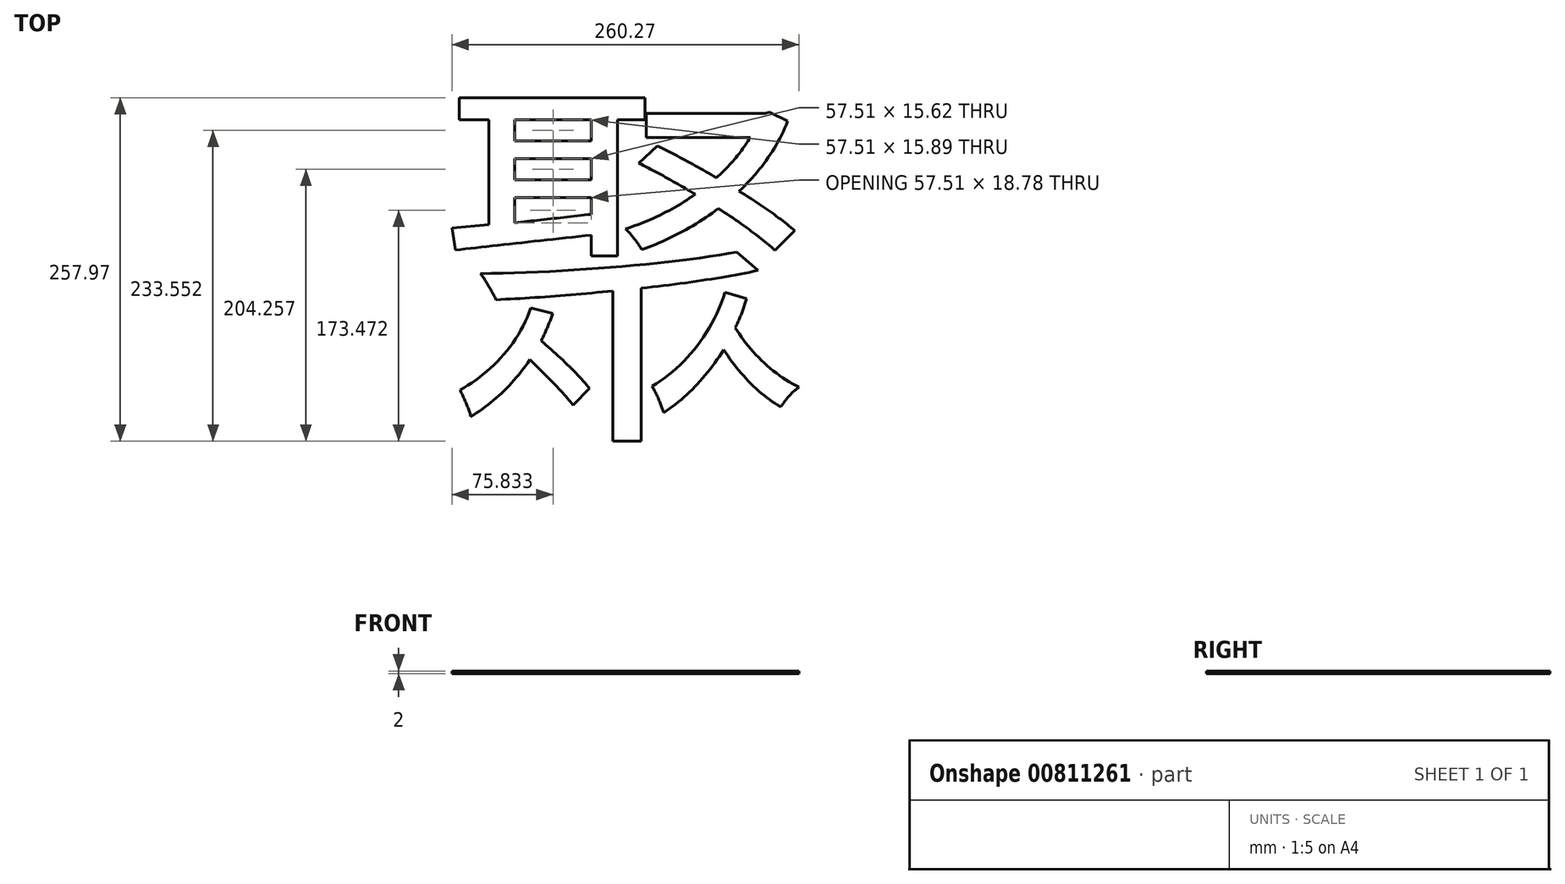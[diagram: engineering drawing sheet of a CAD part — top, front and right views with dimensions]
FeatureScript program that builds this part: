
annotation { "Feature Type Name" : "Feature", "Feature Type Description" : "" }
export const myFeature = defineFeature(function(context is Context, id is Id, definition is map)
    precondition{}
    {
        {
            var Q0;
            Q0=qCreatedBy(makeId("Top.planeOp"),FACE);
            var sketch = newSketch(context, id + "F0", { "sketchPlane" : qUnion([Q0])});
            skText(sketch, "E0", { "text": "聚", "fontName": "NotoSansCJKtc-Regular.otf"});
            const initialGuessF0  = {"E0": [0, 0, 1, 0, 0.208]};
            skSetInitialGuess(sketch, initialGuessF0);
            skSolve(sketch);
        }
        {
            var Q0;
            Q0 = qSketchRegion(id + "F0", true);
            extrude(context, id + "F1", {"entities" : qUnion([Q0]), "depth" : 2 * mm, "offsetDistance" : 25.4 * mm});
        }
    });
